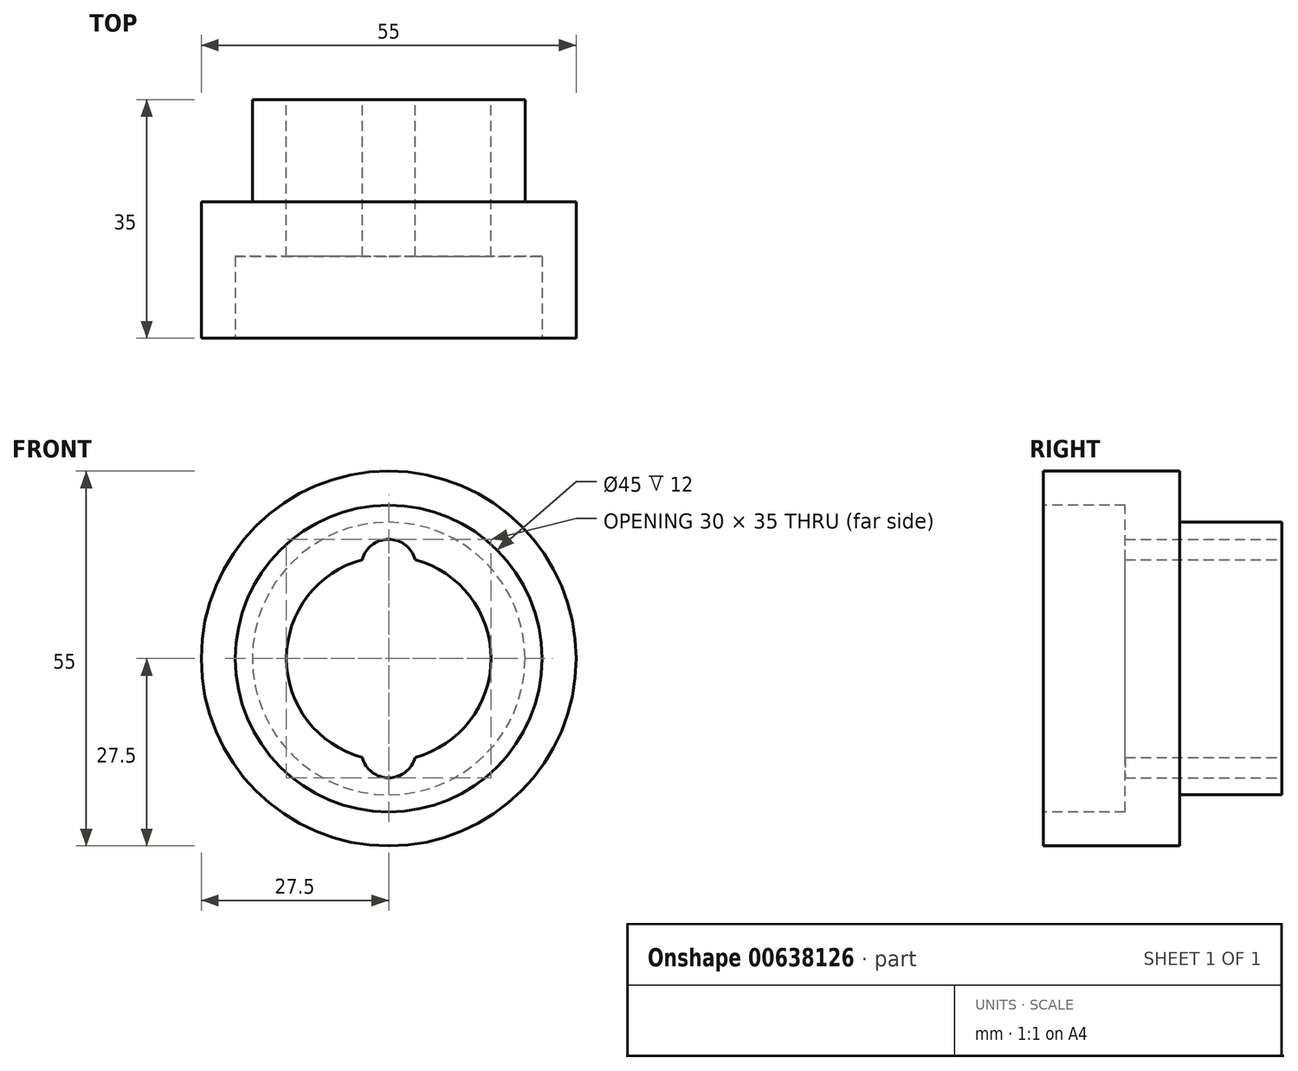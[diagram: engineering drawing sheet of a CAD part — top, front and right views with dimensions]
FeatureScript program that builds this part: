
annotation { "Feature Type Name" : "Feature", "Feature Type Description" : "" }
export const myFeature = defineFeature(function(context is Context, id is Id, definition is map)
    precondition{}
    {
        {
            var Q0;
            Q0=qCreatedBy(makeId("Front.planeOp"),FACE);
            var sketch = newSketch(context, id + "F0", { "sketchPlane" : qUnion([Q0])});
            skCircle(sketch, "E0", {"center": v(0, 0) * mm, "radius": 15 * mm});
            skCircle(sketch, "E1", {"center": v(0, 0) * mm, "radius": 20 * mm});
            skLineSegment(sketch, "E2", {"start": v(-4, 13.5) * mm, "end": v(4, 13.5) * mm});
            skArc(sketch, "E3", {"start": v(4, 13.5) * mm, "mid": v(0, 17.5) * mm, "end": v(-4, 13.5) * mm});
            skArc(sketch, "E4.MirrorCS", {"start": v(4, -13.5) * mm, "mid": v(0, -17.5) * mm, "end": v(-4, -13.5) * mm});
            skLineSegment(sketch, "E5.MirrorCS", {"start": v(-4, -13.5) * mm, "end": v(4, -13.5) * mm});
            skSolve(sketch);
        }
        {
            var Q0;
            Q0 = qSketchRegion(id + "F0", true);
            extrude(context, id + "F1", {"entities" : qUnion([Q0]), "depth" : 35 * mm, "offsetDistance" : 25 * mm});
        }
        {
            var Q0;
            Q0=makeQuery(id+"F1.opExtrude","CAP_FACE",FACE,{"disambiguationData":[OSD([sQuery(id+"F0.wireOp",EDGE,"E0"),sQuery(id+"F0.wireOp",EDGE,"E1"),sQuery(id+"F0.wireOp",EDGE,"E3"),sQuery(id+"F0.wireOp",EDGE,"E4.MirrorCS")])],"isStart":false});
            var sketch = newSketch(context, id + "F2", { "sketchPlane" : qUnion([Q0])});
            skCircle(sketch, "E6", {"center": v(0, 0) * mm, "radius": 27.5 * mm});
            skCircle(sketch, "E7", {"center": v(0, 0) * mm, "radius": 20 * mm});
            skSolve(sketch);
        }
        {
            var Q0;
            Q0 = qSketchRegion(id + "F2", true);
            extrude(context, id + "F3", {"entities" : qUnion([Q0]), "operationType" : NewBodyOperationType.ADD, "oppositeDirection" : true, "depth" : 20 * mm, "offsetDistance" : 25 * mm});
        }
        {
            var Q0;
            Q0=makeQuery(id+"F3.boolean.opBoolean","MERGE",FACE,{"derivedFrom":[makeQuery(id+"F1.opExtrude","CAP_FACE",FACE,{"disambiguationData":[OSD([sQuery(id+"F0.wireOp",EDGE,"E0"),sQuery(id+"F0.wireOp",EDGE,"E1"),sQuery(id+"F0.wireOp",EDGE,"E3"),sQuery(id+"F0.wireOp",EDGE,"E4.MirrorCS")])],"isStart":false}),makeQuery(id+"F3.opExtrude","CAP_FACE",FACE,{"disambiguationData":[OSD([sQuery(id+"F2.wireOp",EDGE,"E6"),sQuery(id+"F2.wireOp",EDGE,"E7")])],"isStart":true})]});
            var sketch = newSketch(context, id + "F4", { "sketchPlane" : qUnion([Q0])});
            skCircle(sketch, "E8", {"center": v(0, 0) * mm, "radius": 22.5 * mm});
            skSolve(sketch);
        }
        {
            var Q0;
            Q0 = qSketchRegion(id + "F4", true);
            extrude(context, id + "F5", {"entities" : qUnion([Q0]), "operationType" : NewBodyOperationType.REMOVE, "oppositeDirection" : true, "depth" : 12 * mm, "offsetDistance" : 25 * mm});
        }
    });
